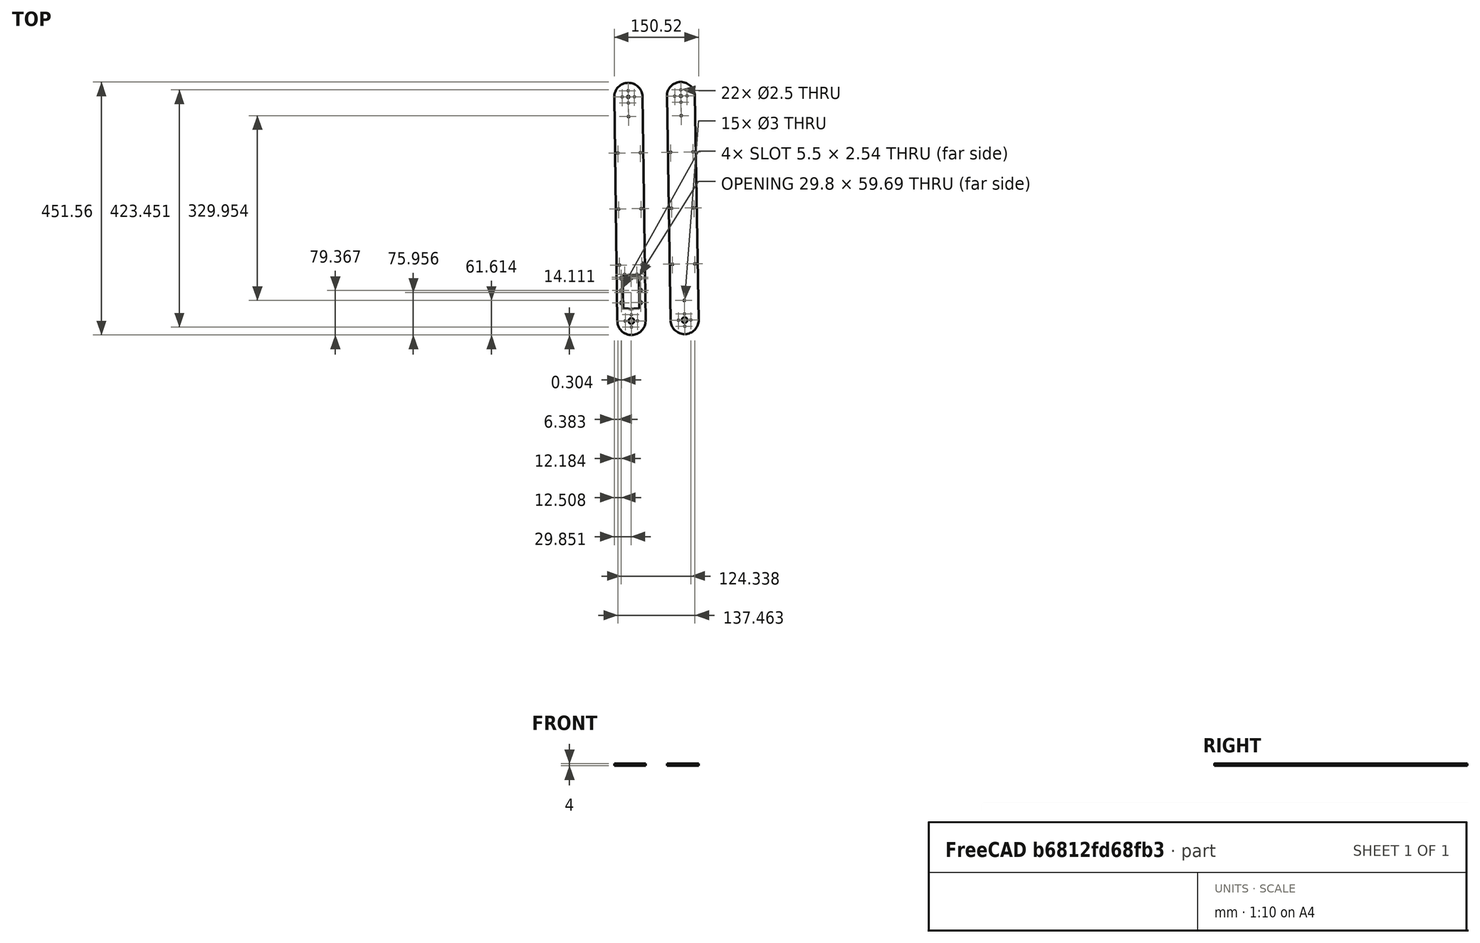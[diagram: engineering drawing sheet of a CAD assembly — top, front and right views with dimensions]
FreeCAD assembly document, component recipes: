
FREECAD ASSEMBLY — COMPONENT RECIPES ("arm_assembly_def2")

This assembly document has 2 components, labeled P0..P1 below (a component is one placed body or linked part). 2 of them carry a construction recipe — the FreeCAD feature program that regenerates the part from scratch, quoted from this document or its linked companion documents; the rest are supplied as boundary geometry only. No exploded tour is included for this assembly.
COMPONENT P0 — recipe-attached ("arm_low_1", modeled in this document).
Construction recipe (the document's own serialized feature program — sketch geometry with constraints, then the solid features built on it; lengths are millimeters unless a unit is written):

FEATURE [Sketcher::SketchObject] Sketch
  ArcFitTolerance = 1e-06
  AttachmentSupport = -> [XY_Plane]
  FullyConstrained = false
  MakeInternals = false
  MapMode = 5
  sketch-geometry (101):
    g0: LineSegment [constr] StartX=1.5008e-12 StartY=20 StartZ=0 EndX=1.5008e-12 EndY=-20 EndZ=0
    g1: LineSegment [constr] StartX=0 StartY=0 StartZ=0 EndX=0 EndY=400 EndZ=0
    g2: LineSegment [constr] StartX=1.5008e-12 StartY=20 StartZ=0 EndX=1.5008e-12 EndY=25 EndZ=0
    g3: Circle CenterX=0 CenterY=400 CenterZ=0 NormalX=0 NormalY=0 NormalZ=1 AngleXU=0 Radius=2
    g4: Circle CenterX=-10.9997 CenterY=400 CenterZ=0 NormalX=0 NormalY=0 NormalZ=1 AngleXU=0 Radius=1.25
    g5: Circle CenterX=0 CenterY=389 CenterZ=0 NormalX=0 NormalY=0 NormalZ=1 AngleXU=0 Radius=1.25
    g6: Circle CenterX=10.9997 CenterY=400 CenterZ=0 NormalX=0 NormalY=0 NormalZ=1 AngleXU=0 Radius=1.25
    g7: Circle CenterX=0 CenterY=411 CenterZ=0 NormalX=0 NormalY=0 NormalZ=1 AngleXU=0 Radius=1.25
    g8: LineSegment [constr] StartX=0 StartY=-5 StartZ=0 EndX=0 EndY=5.99996 EndZ=0
    g9: Circle [constr] CenterX=0 CenterY=0 CenterZ=0 NormalX=0 NormalY=0 NormalZ=1 AngleXU=0 Radius=14
    g10: LineSegment [constr] StartX=0 StartY=0 StartZ=0 EndX=25.23 EndY=0 EndZ=0
    g11: Circle [constr] CenterX=0 CenterY=-3.8e-05 CenterZ=0 NormalX=0 NormalY=0 NormalZ=1 AngleXU=0 Radius=11
    g12: Circle CenterX=0 CenterY=0 CenterZ=0 NormalX=0 NormalY=0 NormalZ=1 AngleXU=0 Radius=5
    g13: Circle CenterX=10.9997 CenterY=0 CenterZ=0 NormalX=0 NormalY=0 NormalZ=1 AngleXU=0 Radius=1.25
    g14: Circle CenterX=-10.9997 CenterY=0 CenterZ=0 NormalX=0 NormalY=0 NormalZ=1 AngleXU=0 Radius=1.25
    g15: Circle CenterX=0 CenterY=-10.9997 CenterZ=0 NormalX=0 NormalY=0 NormalZ=1 AngleXU=0 Radius=1.25
    g16: Circle CenterX=0 CenterY=11 CenterZ=0 NormalX=0 NormalY=0 NormalZ=1 AngleXU=0 Radius=1.25
    g17: LineSegment [constr] StartX=0 StartY=0 StartZ=0 EndX=-25 EndY=0 EndZ=0
    g18: LineSegment [constr] StartX=20.1368 StartY=86.1 StartZ=0 EndX=20.1368 EndY=25 EndZ=0
    g19: LineSegment [constr] StartX=0.036848 StartY=80.5 StartZ=0 EndX=14.5368 EndY=80.5 EndZ=0
    g20: LineSegment StartX=14.5368 StartY=80.5 StartZ=0 EndX=-14.4632 EndY=80.5 EndZ=0
    g21: LineSegment StartX=14.5368 StartY=80.5 StartZ=0 EndX=14.5368 EndY=25 EndZ=0
    g22: Circle CenterX=11.0368 CenterY=83.3 CenterZ=0 NormalX=0 NormalY=0 NormalZ=1 AngleXU=0 Radius=1.25
    g23: Circle CenterX=17.3368 CenterY=78 CenterZ=0 NormalX=0 NormalY=0 NormalZ=1 AngleXU=0 Radius=1.25
    g24: LineSegment [constr] StartX=-20.0632 StartY=86.1 StartZ=0 EndX=20.1368 EndY=86.1 EndZ=0
    g25: Circle [constr] CenterX=17.3368 CenterY=56.0002 CenterZ=0 NormalX=0 NormalY=0 NormalZ=1 AngleXU=0 Radius=1.25
    g26: Circle [constr] CenterX=17.3368 CenterY=34 CenterZ=0 NormalX=0 NormalY=0 NormalZ=1 AngleXU=0 Radius=1.25
    g27: Circle [constr] CenterX=0.036848 CenterY=38 CenterZ=0 NormalX=0 NormalY=0 NormalZ=1 AngleXU=0 Radius=14
    g28: ArcOfCircle [constr] CenterX=0.036848 CenterY=38 CenterZ=0 NormalX=0 NormalY=0 NormalZ=1 AngleXU=0 Radius=14 StartAngle=4.33214 EndAngle=5.09264
    g29: LineSegment [constr] StartX=5.233 StartY=25 StartZ=0 EndX=14.5368 EndY=25 EndZ=0
    g30: LineSegment [constr] StartX=14.5368 StartY=25 StartZ=0 EndX=20.1368 EndY=25 EndZ=0
    g31: LineSegment [constr] StartX=17.3368 StartY=56.0002 StartZ=0 EndX=-17.2632 EndY=56.0002 EndZ=0
    g32: LineSegment [constr] StartX=-20.0632 StartY=25 StartZ=0 EndX=-20.0632 EndY=86.1 EndZ=0
    g33: LineSegment StartX=-14.4632 StartY=80.5 StartZ=0 EndX=-14.4632 EndY=25 EndZ=0
    g34: Circle CenterX=-17.2632 CenterY=78 CenterZ=0 NormalX=0 NormalY=0 NormalZ=1 AngleXU=0 Radius=1.25
    g35: Circle CenterX=-10.9632 CenterY=83.3 CenterZ=0 NormalX=0 NormalY=0 NormalZ=1 AngleXU=0 Radius=1.25
    g36: Circle [constr] CenterX=-17.2632 CenterY=56.0002 CenterZ=0 NormalX=0 NormalY=0 NormalZ=1 AngleXU=0 Radius=1.25
    g37: Circle [constr] CenterX=-17.2632 CenterY=34 CenterZ=0 NormalX=0 NormalY=0 NormalZ=1 AngleXU=0 Radius=1.25
    g38: LineSegment [constr] StartX=-14.4632 StartY=25 StartZ=0 EndX=-5.15931 EndY=25 EndZ=0
    g39: LineSegment [constr] StartX=-20.0632 StartY=25 StartZ=0 EndX=-14.4632 EndY=25 EndZ=0
    g40: ArcOfCircle CenterX=0.115002 CenterY=3.75548e-06 CenterZ=0 NormalX=0 NormalY=0 NormalZ=1 AngleXU=0 Radius=25.115 StartAngle=3.14159 EndAngle=6.28319
    g41: ArcOfCircle CenterX=0.115002 CenterY=399.959 CenterZ=0 NormalX=0 NormalY=0 NormalZ=1 AngleXU=0 Radius=25.115 StartAngle=0 EndAngle=3.14159
    g42: LineSegment StartX=-25 StartY=3.75548e-06 StartZ=0 EndX=-25 EndY=399.959 EndZ=0
    g43: LineSegment StartX=25.23 StartY=3.75548e-06 StartZ=0 EndX=25.23 EndY=399.959 EndZ=0
    g44: LineSegment [constr] StartX=25.23 StartY=199.98 StartZ=0 EndX=-25 EndY=199.98 EndZ=0
    g45: LineSegment [constr] StartX=25.23 StartY=199.98 StartZ=0 EndX=55.23 EndY=199.98 EndZ=0
    g46: LineSegment [constr] StartX=25.23 StartY=0 StartZ=0 EndX=55.23 EndY=0 EndZ=0
    g47: LineSegment [constr] StartX=55.23 StartY=0 StartZ=0 EndX=55.23 EndY=199.98 EndZ=0
    g48: LineSegment [constr] StartX=55.23 StartY=99.9898 StartZ=0 EndX=25.23 EndY=99.9898 EndZ=0
    g49: LineSegment [constr] StartX=25.23 StartY=99.9898 StartZ=0 EndX=-25 EndY=99.9898 EndZ=0
    g50: LineSegment [constr] StartX=25.23 StartY=399.959 StartZ=0 EndX=55.23 EndY=399.959 EndZ=0
    g51: LineSegment [constr] StartX=55.23 StartY=399.959 StartZ=0 EndX=55.23 EndY=199.98 EndZ=0
    g52: LineSegment [constr] StartX=55.23 StartY=299.969 StartZ=0 EndX=25.23 EndY=299.969 EndZ=0
    g53: LineSegment [constr] StartX=25.23 StartY=299.969 StartZ=0 EndX=-25 EndY=299.969 EndZ=0
    g54: LineSegment [constr] StartX=-25 StartY=299.969 StartZ=0 EndX=-20 EndY=299.969 EndZ=0
    g55: LineSegment [constr] StartX=-20 StartY=299.969 StartZ=0 EndX=-20 EndY=199.98 EndZ=0
    g56: LineSegment [constr] StartX=-20 StartY=199.98 StartZ=0 EndX=-20 EndY=99.9898 EndZ=0
    g57: LineSegment [constr] StartX=25.23 StartY=299.969 StartZ=0 EndX=20.23 EndY=299.969 EndZ=0
    g58: LineSegment [constr] StartX=20.23 StartY=299.969 StartZ=0 EndX=20.23 EndY=199.98 EndZ=0
    g59: LineSegment [constr] StartX=20.23 StartY=199.98 StartZ=0 EndX=20.23 EndY=99.9898 EndZ=0
    g60: Circle CenterX=-20 CenterY=299.969 CenterZ=0 NormalX=0 NormalY=0 NormalZ=1 AngleXU=0 Radius=1.5
    g61: Circle CenterX=20.23 CenterY=299.969 CenterZ=0 NormalX=0 NormalY=0 NormalZ=1 AngleXU=0 Radius=1.5
    g62: Circle CenterX=-20 CenterY=199.98 CenterZ=0 NormalX=0 NormalY=0 NormalZ=1 AngleXU=0 Radius=1.5
    g63: Circle CenterX=20.23 CenterY=199.98 CenterZ=0 NormalX=0 NormalY=0 NormalZ=1 AngleXU=0 Radius=1.5
    g64: Circle CenterX=-20 CenterY=99.9898 CenterZ=0 NormalX=0 NormalY=0 NormalZ=1 AngleXU=0 Radius=1.5
    g65: Circle CenterX=20.23 CenterY=99.9898 CenterZ=0 NormalX=0 NormalY=0 NormalZ=1 AngleXU=0 Radius=1.5
    g66: LineSegment [constr] StartX=-17.2632 StartY=34 StartZ=0 EndX=17.3368 EndY=34 EndZ=0
    g67: LineSegment [constr] StartX=-17.2632 StartY=34 StartZ=0 EndX=-17.2632 EndY=31 EndZ=0
    g68: LineSegment [constr] StartX=17.3368 StartY=34 StartZ=0 EndX=17.3368 EndY=31 EndZ=0
    g69: ArcOfCircle CenterX=-17.2632 CenterY=34 CenterZ=0 NormalX=0 NormalY=0 NormalZ=1 AngleXU=0 Radius=1.25 StartAngle=1.93e-14 EndAngle=3.14159
    g70: ArcOfCircle CenterX=-17.2632 CenterY=31 CenterZ=0 NormalX=0 NormalY=0 NormalZ=1 AngleXU=0 Radius=1.25 StartAngle=3.14159 EndAngle=6.28319
    g71: LineSegment StartX=-16.0132 StartY=34 StartZ=0 EndX=-16.0132 EndY=31 EndZ=0
    g72: LineSegment StartX=-18.5132 StartY=34 StartZ=0 EndX=-18.5132 EndY=31 EndZ=0
    g73: ArcOfCircle CenterX=17.3368 CenterY=34 CenterZ=0 NormalX=0 NormalY=0 NormalZ=1 AngleXU=0 Radius=1.25 StartAngle=1e-16 EndAngle=3.14159
    g74: ArcOfCircle CenterX=17.3368 CenterY=31 CenterZ=0 NormalX=0 NormalY=0 NormalZ=1 AngleXU=0 Radius=1.25 StartAngle=3.14159 EndAngle=6.28319
    g75: LineSegment StartX=18.5868 StartY=34 StartZ=0 EndX=18.5868 EndY=31 EndZ=0
    g76: LineSegment StartX=16.0868 StartY=34 StartZ=0 EndX=16.0868 EndY=31 EndZ=0
    g77: LineSegment [constr] StartX=-17.2632 StartY=78 StartZ=0 EndX=17.3368 EndY=78 EndZ=0
    g78: LineSegment [constr] StartX=-17.2632 StartY=78 StartZ=0 EndX=-17.2632 EndY=75 EndZ=0
    g79: Circle CenterX=-17.2632 CenterY=75 CenterZ=0 NormalX=0 NormalY=0 NormalZ=1 AngleXU=0 Radius=1.25
    g80: LineSegment [constr] StartX=17.3368 StartY=78 StartZ=0 EndX=17.3368 EndY=75 EndZ=0
    g81: Circle CenterX=17.3368 CenterY=75 CenterZ=0 NormalX=0 NormalY=0 NormalZ=1 AngleXU=0 Radius=1.25
    g82: LineSegment StartX=-14.4632 StartY=25 StartZ=0 EndX=-14.4632 EndY=22 EndZ=0
    g83: LineSegment StartX=14.5368 StartY=25 StartZ=0 EndX=14.5368 EndY=22 EndZ=0
    g84: LineSegment StartX=5.233 StartY=22 StartZ=0 EndX=14.5368 EndY=22 EndZ=0
    g85: ArcOfCircle CenterX=0.036848 CenterY=35 CenterZ=0 NormalX=0 NormalY=0 NormalZ=1 AngleXU=0 Radius=14 StartAngle=4.33214 EndAngle=5.09264
    g86: LineSegment StartX=-14.4632 StartY=22 StartZ=0 EndX=-5.15931 EndY=22 EndZ=0
    g87: LineSegment [constr] StartX=-17.2632 StartY=56.0002 StartZ=0 EndX=-17.2632 EndY=53.0002 EndZ=0
    g88: LineSegment [constr] StartX=17.3368 StartY=56.0002 StartZ=0 EndX=17.3368 EndY=53.0002 EndZ=0
    g89: ArcOfCircle CenterX=-17.2632 CenterY=56.0002 CenterZ=0 NormalX=0 NormalY=0 NormalZ=1 AngleXU=0 Radius=1.25 StartAngle=1.93e-14 EndAngle=3.14159
    g90: ArcOfCircle CenterX=-17.2632 CenterY=53.0002 CenterZ=0 NormalX=0 NormalY=0 NormalZ=1 AngleXU=0 Radius=1.25 StartAngle=3.14159 EndAngle=6.28319
    g91: LineSegment StartX=-16.0132 StartY=56.0002 StartZ=0 EndX=-16.0132 EndY=53.0002 EndZ=0
    g92: LineSegment StartX=-18.5132 StartY=56.0002 StartZ=0 EndX=-18.5132 EndY=53.0002 EndZ=0
    g93: ArcOfCircle CenterX=17.3368 CenterY=56.0002 CenterZ=0 NormalX=0 NormalY=0 NormalZ=1 AngleXU=0 Radius=1.25 StartAngle=2.46e-14 EndAngle=3.14159
    g94: ArcOfCircle CenterX=17.3368 CenterY=53.0002 CenterZ=0 NormalX=0 NormalY=0 NormalZ=1 AngleXU=0 Radius=1.25 StartAngle=3.14159 EndAngle=6.28319
    g95: LineSegment StartX=18.5868 StartY=56.0002 StartZ=0 EndX=18.5868 EndY=53.0002 EndZ=0
    g96: LineSegment StartX=16.0868 StartY=56.0002 StartZ=0 EndX=16.0868 EndY=53.0002 EndZ=0
    g97: Circle [constr] CenterX=0.115002 CenterY=399.959 CenterZ=0 NormalX=0 NormalY=0 NormalZ=1 AngleXU=0 Radius=25.115
    g98: LineSegment [constr] StartX=0 StartY=400 StartZ=0 EndX=0 EndY=374.844 EndZ=0
    g99: LineSegment [constr] StartX=0 StartY=374.844 StartZ=0 EndX=0 EndY=364.844 EndZ=0
    g100: Circle CenterX=0 CenterY=364.844 CenterZ=0 NormalX=0 NormalY=0 NormalZ=1 AngleXU=0 Radius=1.5
  constraints (211):
    c: Vertical(g0)
    c: Vertical(g1)
    c: Coincident(g2,g0)
    c: Vertical(g2)
    c: Diameter(g3) = 4
    c: Coincident(g3,g1)
    c: Diameter(g7) = 2.5
    c: Diameter(g4) = 2.5
    c: Diameter(g5) = 2.5
    c: Diameter(g6) = 2.5
    c: Vertical(g8)
    c: Diameter(g9) = 28
    c: Coincident(g17,g9)
    c: Horizontal(g17)
    c: Coincident(g10,g9)
    c: Horizontal(g10)
    c: Diameter(g11) = 22
    c: Diameter(g12) = 10
    c: Coincident(g12,g9)
    c: Diameter(g16) = 2.5
    c: Diameter(g14) = 2.5
    c: Diameter(g15) = 2.5
    c: Diameter(g13) = 2.5
    c: Coincident(g24,g18)
    c: Coincident(g32,g24)
    c: Horizontal(g24)
    c: Vertical(g18)
    c: Vertical(g32)
    c: Distance(g18,g32) = 40.2
    c: Distance(g24,g32) = 61.1
    c: Diameter(g28) = 28
    c: Horizontal(g19)
    c: Coincident(g20,g19)
    c: Horizontal(g20)
    c: Coincident(g33,g20)
    c: Vertical(g33)
    c: Coincident(g21,g19)
    c: Vertical(g21)
    c: Diameter(g22) = 2.5
    c: Equal(g22,g35)
    c: Equal(g22,g26)
    c: Equal(g22,g37)
    c: Equal(g22,g36)
    c: Equal(g22,g34)
    c: Equal(g22,g23)
    c: Equal(g22,g25)
    c: Coincident(g27,g28)
    c: PointOnObject(g28,g27)
    c: Coincident(g29,g28)
    c: Coincident(g29,g21)
    c: Horizontal(g29)
    c: Coincident(g30,g21)
    c: Coincident(g30,g18)
    c: Horizontal(g30)
    c: Coincident(g38,g33)
    c: Coincident(g38,g28)
    c: Horizontal(g38)
    c: Coincident(g39,g32)
    c: Coincident(g39,g33)
    c: Horizontal(g39)
    c: Coincident(g31,g25)
    c: Coincident(g31,g36)
    c: Horizontal(g31)
    c: DistanceY(g27,g1) = 362
    c: Tangent(g40,g42) = 1.5708
    c: Tangent(g40,g43) = -1.5708
    c: Tangent(g41,g42) = 1.5708
    c: Tangent(g41,g43) = -1.5708
    c: Equal(g40,g41)
    c: Symmetric(g43,g43,g44)
    c: Symmetric(g42,g42,g44)
    c: Horizontal(g44)
    c: Distance(g45) = 30
    c: Horizontal(g45)
    c: Coincident(g45,g44)
    c: Distance(g46) = 30
    c: Horizontal(g46)
    c: Coincident(g46,g10)
    c: PointOnObject(g46,g-1)
    c: Coincident(g47,g46)
    c: Coincident(g47,g45)
    c: Vertical(g47)
    c: Symmetric(g47,g47,g48)
    c: PointOnObject(g48,g43)
    c: Horizontal(g48)
    c: Coincident(g49,g48)
    c: PointOnObject(g49,g42)
    c: Horizontal(g49)
    c: Distance(g50) = 30
    c: Horizontal(g50)
    c: Coincident(g50,g41)
    c: Coincident(g51,g50)
    c: Coincident(g51,g45)
    c: Symmetric(g51,g51,g52)
    c: PointOnObject(g52,g43)
    c: Horizontal(g52)
    c: Coincident(g53,g52)
    c: PointOnObject(g53,g42)
    c: Horizontal(g53)
    c: Distance(g54) = 5
    c: Coincident(g54,g53)
    c: PointOnObject(g54,g53)
    c: Coincident(g55,g54)
    c: PointOnObject(g55,g44)
    c: Vertical(g55)
    c: Coincident(g56,g55)
    c: PointOnObject(g56,g49)
    c: Vertical(g56)
    c: Distance(g57) = 5
    c: Coincident(g57,g52)
    c: PointOnObject(g57,g53)
    c: Coincident(g58,g57)
    c: PointOnObject(g58,g44)
    c: Vertical(g58)
    c: Coincident(g59,g58)
    c: PointOnObject(g59,g49)
    c: Vertical(g59)
    c: Coincident(g60,g54)
    c: Diameter(g60) = 3
    c: Coincident(g61,g57)
    c: Equal(g60,g61)
    c: Coincident(g62,g55)
    c: Equal(g60,g62)
    c: Coincident(g63,g58)
    c: Equal(g62,g63)
    c: Coincident(g64,g56)
    c: Equal(g62,g64)
    c: Coincident(g65,g59)
    c: Equal(g64,g65)
    c: DistanceY(g40,g27) = 38
    c: Coincident(g66,g37)
    c: Coincident(g66,g26)
    c: Horizontal(g66)
    c: DistanceX(g66,g66) = 34.6
    c: Distance(g67) = 3
    c: Coincident(g67,g37)
    c: Vertical(g67)
    c: Distance(g68) = 3
    c: Coincident(g68,g26)
    c: Vertical(g68)
    c: Tangent(g69,g71) = 1.5708
    c: Tangent(g69,g72) = -1.5708
    c: Tangent(g70,g71) = 1.5708
    c: Tangent(g70,g72) = -1.5708
    c: Equal(g69,g70)
    c: Radius(g69) = 1.25
    c: Coincident(g69,g37)
    c: Coincident(g70,g67)
    c: Tangent(g73,g75) = 1.5708
    c: Tangent(g73,g76) = -1.5708
    c: Tangent(g74,g75) = 1.5708
    c: Tangent(g74,g76) = -1.5708
    c: Equal(g73,g74)
    c: Coincident(g77,g34)
    c: Coincident(g77,g23)
    c: Horizontal(g77)
    c: DistanceX(g77,g77) = 34.6
    c: Distance(g78) = 3
    c: Coincident(g78,g34)
    c: Vertical(g78)
    c: Coincident(g79,g78)
    c: Equal(g79,g34)
    c: Distance(g80) = 3
    c: Coincident(g80,g23)
    c: Vertical(g80)
    c: Coincident(g81,g80)
    c: Equal(g81,g23)
    c: DistanceX(g33,g21) = 29
    c: Distance(g82) = 3
    c: Coincident(g82,g33)
    c: Vertical(g82)
    c: Distance(g83) = 3
    c: Coincident(g83,g21)
    c: Vertical(g83)
    c: Diameter(g85) = 28
    c: Coincident(g84,g85)
    c: Horizontal(g84)
    c: Coincident(g86,g85)
    c: Horizontal(g86)
    c: DistanceX(g31,g31) = 34.6
    c: Distance(g87) = 3
    c: Coincident(g87,g31)
    c: Vertical(g87)
    c: Distance(g88) = 3
    c: Coincident(g88,g25)
    c: Vertical(g88)
    c: Tangent(g89,g91) = 1.5708
    c: Tangent(g89,g92) = -1.5708
    c: Tangent(g90,g91) = 1.5708
    c: Tangent(g90,g92) = -1.5708
    c: Equal(g89,g90)
    c: Radius(g89) = 1.25
    c: Coincident(g89,g31)
    c: Coincident(g90,g87)
    c: Tangent(g93,g95) = 1.5708
    c: Tangent(g93,g96) = -1.5708
    c: Tangent(g94,g95) = 1.5708
    c: Tangent(g94,g96) = -1.5708
    c: Equal(g93,g94)
    c: Coincident(g97,g41)
    c: PointOnObject(g41,g97)
    c: DistanceX(g1) = 0
    c: DistanceY(g1) = 400
    c: Coincident(g98,g1)
    c: PointOnObject(g98,g97)
    c: Vertical(g98)
    c: Distance(g99) = 10
    c: Coincident(g99,g98)
    c: PointOnObject(g99,g1)
    c: Diameter(g100) = 3
    c: Coincident(g100,g99)
FEATURE [PartDesign::Pad] Pad
  Direction = (0,0,1)
  Length = 4
  Length2 = 10
  Profile = -> Sketch
  ReferenceAxis = -> Sketch [N_Axis]
  Refine = true
  Suppressed = false
  Type = 0
FEATURE [PartDesign::Body] Body  label="arm_low_1"
  AllowCompound = false
  Group = -> [Sketch,Pad]
  Origin = -> Origin
  Placement = pos=(-19.8181,9.93988,17.6558) rot=(0,0,1;0.013804rad)
  Tip = -> Pad
COMPONENT P1 — recipe-attached ("arm_high_1", modeled in this document).
Construction recipe (the document's own serialized feature program — sketch geometry with constraints, then the solid features built on it; lengths are millimeters unless a unit is written):

FEATURE [Sketcher::SketchObject] Sketch001
  ArcFitTolerance = 1e-06
  FullyConstrained = false
  MakeInternals = false
  MapMode = 5
  sketch-geometry (47):
    g0: Circle [constr] CenterX=0 CenterY=0.000303 CenterZ=0 NormalX=0 NormalY=0 NormalZ=1 AngleXU=0 Radius=14
    g1: LineSegment [constr] StartX=0 StartY=0.000303 StartZ=0 EndX=0 EndY=400.001 EndZ=0
    g2: Circle CenterX=0 CenterY=400.001 CenterZ=0 NormalX=0 NormalY=0 NormalZ=1 AngleXU=0 Radius=5
    g3: Circle CenterX=0 CenterY=0.000303 CenterZ=0 NormalX=0 NormalY=0 NormalZ=1 AngleXU=0 Radius=2
    g4: Circle [constr] CenterX=0 CenterY=0 CenterZ=0 NormalX=0 NormalY=0 NormalZ=1 AngleXU=0 Radius=11
    g5: ArcOfCircle CenterX=0 CenterY=0 CenterZ=0 NormalX=0 NormalY=0 NormalZ=1 AngleXU=0 Radius=25 StartAngle=3.14159 EndAngle=6.28319
    g6: ArcOfCircle CenterX=0 CenterY=400.001 CenterZ=0 NormalX=0 NormalY=0 NormalZ=1 AngleXU=0 Radius=25 StartAngle=6e-16 EndAngle=3.14159
    g7: LineSegment StartX=-25 StartY=-8e-15 StartZ=0 EndX=-25 EndY=400.001 EndZ=0
    g8: LineSegment StartX=25 StartY=0 StartZ=0 EndX=25 EndY=400.001 EndZ=0
    g9: Circle CenterX=10.9997 CenterY=400.001 CenterZ=0 NormalX=0 NormalY=0 NormalZ=1 AngleXU=0 Radius=1.25
    g10: Circle CenterX=0 CenterY=411.001 CenterZ=0 NormalX=0 NormalY=0 NormalZ=1 AngleXU=0 Radius=1.25
    g11: Circle CenterX=-10.9997 CenterY=400.001 CenterZ=0 NormalX=0 NormalY=0 NormalZ=1 AngleXU=0 Radius=1.25
    g12: Circle CenterX=0 CenterY=389.001 CenterZ=0 NormalX=0 NormalY=0 NormalZ=1 AngleXU=0 Radius=1.25
    g13: Circle CenterX=10.9997 CenterY=0.000303 CenterZ=0 NormalX=0 NormalY=0 NormalZ=1 AngleXU=0 Radius=1.25
    g14: Circle CenterX=0 CenterY=11 CenterZ=0 NormalX=0 NormalY=0 NormalZ=1 AngleXU=0 Radius=1.25
    g15: Circle CenterX=-10.9997 CenterY=0.000303 CenterZ=0 NormalX=0 NormalY=0 NormalZ=1 AngleXU=0 Radius=1.25
    g16: Circle CenterX=0 CenterY=-10.9994 CenterZ=0 NormalX=0 NormalY=0 NormalZ=1 AngleXU=0 Radius=1.25
    g17: LineSegment [constr] StartX=25 StartY=200 StartZ=0 EndX=-25 EndY=200 EndZ=0
    g18: LineSegment [constr] StartX=25 StartY=200 StartZ=0 EndX=55 EndY=200 EndZ=0
    g19: LineSegment [constr] StartX=25 StartY=0 StartZ=0 EndX=55 EndY=0 EndZ=0
    g20: LineSegment [constr] StartX=25 StartY=400.001 StartZ=0 EndX=55 EndY=400.001 EndZ=0
    g21: LineSegment [constr] StartX=55 StartY=200 StartZ=0 EndX=55 EndY=400.001 EndZ=0
    g22: LineSegment [constr] StartX=55 StartY=200 StartZ=0 EndX=55 EndY=0 EndZ=0
    g23: LineSegment [constr] StartX=55 StartY=100 StartZ=0 EndX=25 EndY=100 EndZ=0
    g24: LineSegment [constr] StartX=25 StartY=100 StartZ=0 EndX=-25 EndY=100 EndZ=0
    g25: LineSegment [constr] StartX=55 StartY=300 StartZ=0 EndX=25 EndY=300 EndZ=0
    g26: LineSegment [constr] StartX=25 StartY=300 StartZ=0 EndX=-25 EndY=300 EndZ=0
    g27: LineSegment [constr] StartX=-25 StartY=300 StartZ=0 EndX=-20 EndY=300 EndZ=0
    g28: LineSegment [constr] StartX=-20 StartY=300 StartZ=0 EndX=-20 EndY=200 EndZ=0
    g29: LineSegment [constr] StartX=-20 StartY=200 StartZ=0 EndX=-20 EndY=100 EndZ=0
    g30: LineSegment [constr] StartX=25 StartY=100 StartZ=0 EndX=20 EndY=100 EndZ=0
    g31: LineSegment [constr] StartX=20 StartY=100 StartZ=0 EndX=20 EndY=200 EndZ=0
    g32: LineSegment [constr] StartX=20 StartY=200 StartZ=0 EndX=20 EndY=300 EndZ=0
    g33: Circle CenterX=-20 CenterY=300 CenterZ=0 NormalX=0 NormalY=0 NormalZ=1 AngleXU=0 Radius=1.5
    g34: Circle CenterX=20 CenterY=300 CenterZ=0 NormalX=0 NormalY=0 NormalZ=1 AngleXU=0 Radius=1.5
    g35: Circle CenterX=-20 CenterY=200 CenterZ=0 NormalX=0 NormalY=0 NormalZ=1 AngleXU=0 Radius=1.5
    g36: Circle CenterX=20 CenterY=200 CenterZ=0 NormalX=0 NormalY=0 NormalZ=1 AngleXU=0 Radius=1.5
    g37: Circle CenterX=-20 CenterY=100 CenterZ=0 NormalX=0 NormalY=0 NormalZ=1 AngleXU=0 Radius=1.5
    g38: Circle CenterX=20 CenterY=100 CenterZ=0 NormalX=0 NormalY=0 NormalZ=1 AngleXU=0 Radius=1.5
    g39: Circle [constr] CenterX=0 CenterY=400.001 CenterZ=0 NormalX=0 NormalY=0 NormalZ=1 AngleXU=0 Radius=25
    g40: LineSegment [constr] StartX=0 StartY=400.001 StartZ=0 EndX=0 EndY=375.001 EndZ=0
    g41: LineSegment [constr] StartX=0 StartY=375.001 StartZ=0 EndX=0 EndY=365.001 EndZ=0
    g42: Circle CenterX=0 CenterY=365.001 CenterZ=0 NormalX=0 NormalY=0 NormalZ=1 AngleXU=0 Radius=1.5
    g43: Circle [constr] CenterX=0 CenterY=0 CenterZ=0 NormalX=0 NormalY=0 NormalZ=1 AngleXU=0 Radius=25
    g44: LineSegment [constr] StartX=0 StartY=0 StartZ=0 EndX=0 EndY=25 EndZ=0
    g45: LineSegment [constr] StartX=0 StartY=25 StartZ=0 EndX=0 EndY=35 EndZ=0
    g46: Circle CenterX=0 CenterY=35 CenterZ=0 NormalX=0 NormalY=0 NormalZ=1 AngleXU=0 Radius=1.5
  constraints (103):
    c: Diameter(g0) = 28
    c: Coincident(g1,g0)
    c: Vertical(g1)
    c: Coincident(g2,g1)
    c: Diameter(g3) = 4
    c: Coincident(g3,g0)
    c: Diameter(g4) = 22
    c: Tangent(g5,g7) = 1.5708
    c: Tangent(g5,g8) = -1.5708
    c: Tangent(g6,g7) = 1.5708
    c: Tangent(g6,g8) = -1.5708
    c: Equal(g5,g6)
    c: Radius(g5) = 25
    c: Coincident(g6,g1)
    c: Vertical(g7)
    c: Diameter(g10) = 2.5
    c: Diameter(g11) = 2.5
    c: Diameter(g12) = 2.5
    c: Diameter(g9) = 2.5
    c: Diameter(g14) = 2.5
    c: Diameter(g15) = 2.5
    c: Diameter(g16) = 2.5
    c: Diameter(g13) = 2.5
    c: Symmetric(g8,g8,g17)
    c: Symmetric(g7,g7,g17)
    c: Distance(g18) = 30
    c: Horizontal(g18)
    c: Coincident(g18,g17)
    c: Distance(g19) = 30
    c: Horizontal(g19)
    c: Coincident(g19,g5)
    c: PointOnObject(g19,g-1)
    c: Distance(g20) = 30
    c: Horizontal(g20)
    c: Coincident(g20,g6)
    c: Coincident(g21,g18)
    c: Coincident(g21,g20)
    c: Coincident(g22,g18)
    c: Coincident(g22,g19)
    c: Symmetric(g22,g22,g23)
    c: PointOnObject(g23,g8)
    c: Horizontal(g23)
    c: Coincident(g24,g23)
    c: PointOnObject(g24,g7)
    c: Horizontal(g24)
    c: Symmetric(g21,g21,g25)
    c: PointOnObject(g25,g8)
    c: Horizontal(g25)
    c: Coincident(g26,g25)
    c: PointOnObject(g26,g7)
    c: Horizontal(g26)
    c: Distance(g27) = 5
    c: Horizontal(g27)
    c: Coincident(g27,g26)
    c: Coincident(g28,g27)
    c: PointOnObject(g28,g17)
    c: Vertical(g28)
    c: Coincident(g29,g28)
    c: PointOnObject(g29,g24)
    c: Vertical(g29)
    c: Distance(g30) = 5
    c: Horizontal(g30)
    c: Coincident(g30,g23)
    c: Coincident(g31,g30)
    c: PointOnObject(g31,g17)
    c: Vertical(g31)
    c: Coincident(g32,g31)
    c: PointOnObject(g32,g26)
    c: Vertical(g32)
    c: Diameter(g33) = 3
    c: Coincident(g33,g27)
    c: Coincident(g34,g32)
    c: Equal(g33,g34)
    c: Coincident(g35,g28)
    c: Equal(g33,g35)
    c: Coincident(g36,g31)
    c: Equal(g35,g36)
    c: Coincident(g37,g29)
    c: Equal(g35,g37)
    c: Coincident(g38,g30)
    c: Equal(g37,g38)
    c: DistanceX(g1) = 0
    c: DistanceY(g1) = 400.001
    c: Coincident(g39,g1)
    c: PointOnObject(g6,g39)
    c: Coincident(g40,g1)
    c: PointOnObject(g40,g39)
    c: Vertical(g40)
    c: Distance(g41) = 10
    c: Coincident(g41,g40)
    c: PointOnObject(g41,g1)
    c: Coincident(g43,g5)
    c: PointOnObject(g5,g43)
    c: DistanceX(g4) = 0
    c: DistanceY(g4) = 0
    c: Coincident(g44,g4)
    c: PointOnObject(g44,g43)
    c: Vertical(g44)
    c: Distance(g45) = 10
    c: Coincident(g45,g44)
    c: PointOnObject(g45,g1)
    c: Diameter(g46) = 3
    c: Coincident(g46,g45)
FEATURE [PartDesign::Pad] Pad001
  Direction = (0,0,1)
  Length = 4
  Length2 = 10
  Profile = -> Sketch001
  ReferenceAxis = -> Sketch001 [N_Axis]
  Refine = true
  Suppressed = false
  Type = 0
FEATURE [PartDesign::Body] Body001  label="arm_high_1"
  AllowCompound = false
  Group = -> [Sketch001,Pad001]
  Origin = -> Origin001
  Placement = pos=(68.4839,411.394,17.6558) rot=(0,0,1;3.15834rad)
  Tip = -> Pad001
PROVENANCE & LICENSES
A FreeCAD (.FCStd) document from a public repository crawl; recipes are the document's own serialized feature recipes (and, for linked parts, companion documents' recipes).
License: unknown-license-file.
